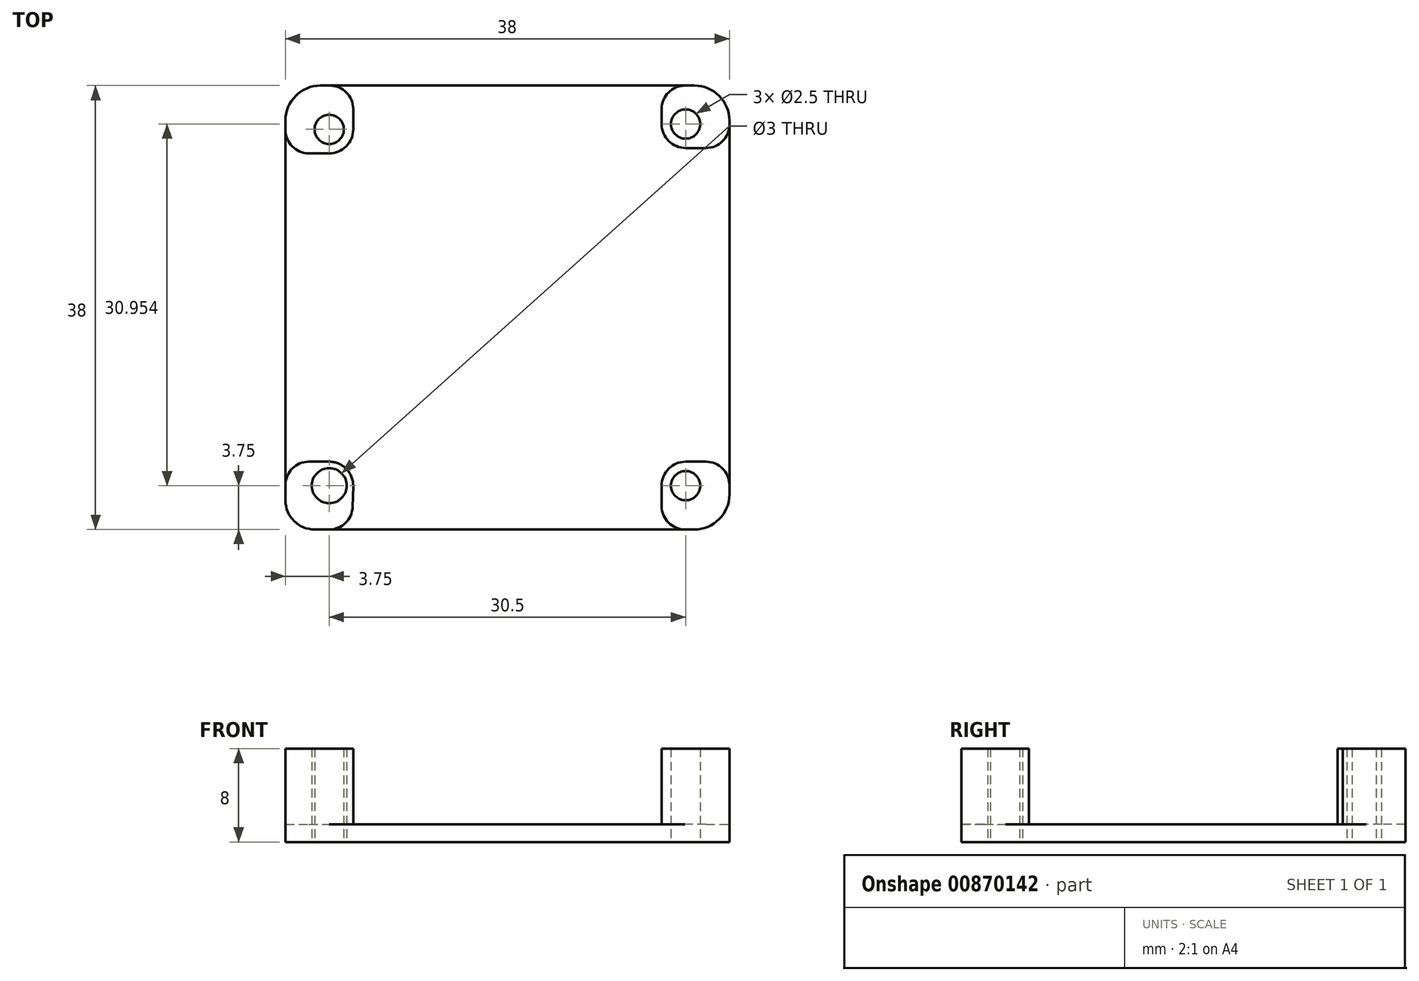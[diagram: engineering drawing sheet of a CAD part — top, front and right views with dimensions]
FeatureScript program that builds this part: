
annotation { "Feature Type Name" : "Feature", "Feature Type Description" : "" }
export const myFeature = defineFeature(function(context is Context, id is Id, definition is map)
    precondition{}
    {
        {
            var Q0;
            Q0=qCreatedBy(makeId("Top.planeOp"),FACE);
            var sketch = newSketch(context, id + "F0", { "sketchPlane" : qUnion([Q0])});
            skLineSegment(sketch, "E0.bottom", {"start": v(16, -19) * mm, "end": v(-16.5, -19) * mm});
            skLineSegment(sketch, "E0.top", {"start": v(16, 19) * mm, "end": v(-16, 19) * mm});
            skLineSegment(sketch, "E0.left", {"start": v(19, -16) * mm, "end": v(19, 16) * mm});
            skLineSegment(sketch, "E0.right", {"start": v(-19, -16.5) * mm, "end": v(-19, 16) * mm});
            skPoint(sketch, "E0.middle", {"position": v(0, 0) * mm});
            skPoint(sketch, "E1", {"position": v(15.25, 15.7) * mm});
            skPoint(sketch, "E2", {"position": v(15.25, -15.25) * mm});
            skPoint(sketch, "E3", {"position": v(-15.25, -15.25) * mm});
            skPoint(sketch, "E4", {"position": v(-15.25, 15.25) * mm});
            skCircle(sketch, "E5", {"center": v(-15.25, 15.25) * mm, "radius": 1.25 * mm});
            skCircle(sketch, "E6", {"center": v(15.25, 15.7) * mm, "radius": 1.25 * mm});
            skCircle(sketch, "E7", {"center": v(15.25, -15.25) * mm, "radius": 1.25 * mm});
            skCircle(sketch, "E8", {"center": v(-15.25, -15.25) * mm, "radius": 1.5 * mm});
            skArc(sketch, "E9", {"start": v(-15.25, 13.2) * mm, "mid": v(-13.8, 13.8) * mm, "end": v(-13.2, 15.25) * mm});
            skArc(sketch, "E10", {"start": v(13.2, 15.7) * mm, "mid": v(13.8, 14.25) * mm, "end": v(15.25, 13.65) * mm});
            skArc(sketch, "E11", {"start": v(-13.2, -15.3) * mm, "mid": v(-13.78, -13.82) * mm, "end": v(-15.25, -13.2) * mm});
            skArc(sketch, "E12", {"start": v(15.25, -13.2) * mm, "mid": v(13.8, -13.8) * mm, "end": v(13.2, -15.25) * mm});
            skLineSegment(sketch, "E13", {"start": v(-15.25, 13.2) * mm, "end": v(-19, 13.2) * mm});
            skLineSegment(sketch, "E14", {"start": v(-13.2, 15.25) * mm, "end": v(-13.2, 19) * mm});
            skLineSegment(sketch, "E15", {"start": v(15.25, 13.65) * mm, "end": v(19, 13.65) * mm});
            skLineSegment(sketch, "E16", {"start": v(13.2, 15.7) * mm, "end": v(13.2, 19) * mm});
            skLineSegment(sketch, "E17", {"start": v(-15.25, -13.2) * mm, "end": v(-19, -13.2) * mm});
            skLineSegment(sketch, "E18", {"start": v(-13.2, -15.3) * mm, "end": v(-13.3, -19) * mm});
            skLineSegment(sketch, "E19", {"start": v(15.25, -13.2) * mm, "end": v(19, -13.2) * mm});
            skLineSegment(sketch, "E20", {"start": v(13.2, -15.25) * mm, "end": v(13.2, -19) * mm});
            skPoint(sketch, "E21.visualSharp", {"position": v(-19, 19) * mm});
            skArc(sketch, "E21.filletArc", {"start": v(-16, 19) * mm, "mid": v(-18.12, 18.12) * mm, "end": v(-19, 16) * mm});
            skPoint(sketch, "E22.visualSharp", {"position": v(19, 19) * mm});
            skArc(sketch, "E22.filletArc", {"start": v(19, 16) * mm, "mid": v(18.12, 18.12) * mm, "end": v(16, 19) * mm});
            skPoint(sketch, "E23.visualSharp", {"position": v(19, -19) * mm});
            skArc(sketch, "E23.filletArc", {"start": v(16, -19) * mm, "mid": v(18.12, -18.12) * mm, "end": v(19, -16) * mm});
            skPoint(sketch, "E24.visualSharp", {"position": v(-19, -19) * mm});
            skArc(sketch, "E24.filletArc", {"start": v(-19, -16.5) * mm, "mid": v(-18.27, -18.27) * mm, "end": v(-16.5, -19) * mm});
            skSolve(sketch);
        }
        {
            var Q0;
            Q0=makeQuery(id+"F0.imprint","IMPRINT",FACE,{"disambiguationData":[TD([[makeQuery(id+"F0.imprint","IMPRINT",EDGE,{"derivedFrom":sQuery(id+"F0.wireOp",EDGE,"E9")}),-1.0]])]});
            var Q1;
            Q1=makeQuery(id+"F0.imprint","IMPRINT",FACE,{"disambiguationData":[TD([[makeQuery(id+"F0.imprint","IMPRINT",EDGE,{"derivedFrom":sQuery(id+"F0.wireOp",EDGE,"E8")}),-1.0]])]});
            var Q2;
            Q2=makeQuery(id+"F0.imprint","IMPRINT",FACE,{"disambiguationData":[TD([[makeQuery(id+"F0.imprint","IMPRINT",EDGE,{"derivedFrom":sQuery(id+"F0.wireOp",EDGE,"E7")}),-1.0]])]});
            var Q3;
            Q3=makeQuery(id+"F0.imprint","IMPRINT",FACE,{"disambiguationData":[TD([[makeQuery(id+"F0.imprint","IMPRINT",EDGE,{"derivedFrom":sQuery(id+"F0.wireOp",EDGE,"E6")}),-1.0]])]});
            var Q4;
            Q4=makeQuery(id+"F0.imprint","IMPRINT",FACE,{"disambiguationData":[TD([[makeQuery(id+"F0.imprint","IMPRINT",EDGE,{"derivedFrom":sQuery(id+"F0.wireOp",EDGE,"E5")}),-1.0]])]});
            extrude(context, id + "F1", {"entities" : qUnion([Q0, Q1, Q2, Q3, Q4]), "depth" : 1.5 * mm, "offsetDistance" : 25 * mm});
        }
        {
            var Q0;
            Q0=makeQuery(id+"F0.imprint","IMPRINT",FACE,{"disambiguationData":[TD([[makeQuery(id+"F0.imprint","IMPRINT",EDGE,{"derivedFrom":sQuery(id+"F0.wireOp",EDGE,"E8")}),-1.0]])]});
            var Q1;
            Q1=makeQuery(id+"F0.imprint","IMPRINT",FACE,{"disambiguationData":[TD([[makeQuery(id+"F0.imprint","IMPRINT",EDGE,{"derivedFrom":sQuery(id+"F0.wireOp",EDGE,"E7")}),-1.0]])]});
            var Q2;
            Q2=makeQuery(id+"F0.imprint","IMPRINT",FACE,{"disambiguationData":[TD([[makeQuery(id+"F0.imprint","IMPRINT",EDGE,{"derivedFrom":sQuery(id+"F0.wireOp",EDGE,"E6")}),-1.0]])]});
            var Q3;
            Q3=makeQuery(id+"F0.imprint","IMPRINT",FACE,{"disambiguationData":[TD([[makeQuery(id+"F0.imprint","IMPRINT",EDGE,{"derivedFrom":sQuery(id+"F0.wireOp",EDGE,"E5")}),-1.0]])]});
            extrude(context, id + "F2", {"entities" : qUnion([Q0, Q1, Q2, Q3]), "operationType" : NewBodyOperationType.ADD, "depth" : 8 * mm, "offsetDistance" : 25 * mm});
        }
        {
            var Q0;
            Q0=makeQuery(id+"F2.opExtrude","SWEPT_EDGE",EDGE,{"disambiguationData":[OSD([sQuery(id+"F0.wireOp",EDGE,"E0.right"),sQuery(id+"F0.wireOp",EDGE,"E13")])]});
            fillet(context, id + "F3", {"entities" : qUnion([Q0]), "radius" : 2 * mm, "tangentPropagation" : true, "allowEdgeOverflow" : false});
        }
        {
            var Q0;
            Q0=makeQuery(id+"F2.opExtrude","SWEPT_EDGE",EDGE,{"disambiguationData":[OSD([sQuery(id+"F0.wireOp",EDGE,"E0.top"),sQuery(id+"F0.wireOp",EDGE,"E14")])]});
            var Q1;
            Q1=makeQuery(id+"F2.opExtrude","SWEPT_EDGE",EDGE,{"disambiguationData":[OSD([sQuery(id+"F0.wireOp",EDGE,"E0.top"),sQuery(id+"F0.wireOp",EDGE,"E16")])]});
            var Q2;
            Q2=makeQuery(id+"F2.opExtrude","SWEPT_EDGE",EDGE,{"disambiguationData":[OSD([sQuery(id+"F0.wireOp",EDGE,"E0.left"),sQuery(id+"F0.wireOp",EDGE,"E15")])]});
            var Q3;
            Q3=makeQuery(id+"F2.opExtrude","SWEPT_EDGE",EDGE,{"disambiguationData":[OSD([sQuery(id+"F0.wireOp",EDGE,"E0.left"),sQuery(id+"F0.wireOp",EDGE,"E19")])]});
            var Q4;
            Q4=makeQuery(id+"F2.opExtrude","SWEPT_EDGE",EDGE,{"disambiguationData":[OSD([sQuery(id+"F0.wireOp",EDGE,"E0.bottom"),sQuery(id+"F0.wireOp",EDGE,"E20")])]});
            var Q5;
            Q5=makeQuery(id+"F2.opExtrude","SWEPT_EDGE",EDGE,{"disambiguationData":[OSD([sQuery(id+"F0.wireOp",EDGE,"E0.bottom"),sQuery(id+"F0.wireOp",EDGE,"E18")])]});
            var Q6;
            Q6=makeQuery(id+"F2.opExtrude","SWEPT_EDGE",EDGE,{"disambiguationData":[OSD([sQuery(id+"F0.wireOp",EDGE,"E0.right"),sQuery(id+"F0.wireOp",EDGE,"E17")])]});
            fillet(context, id + "F4", {"entities" : qUnion([Q0, Q1, Q2, Q3, Q4, Q5, Q6]), "radius" : 2 * mm, "tangentPropagation" : true, "allowEdgeOverflow" : false});
        }
    });
